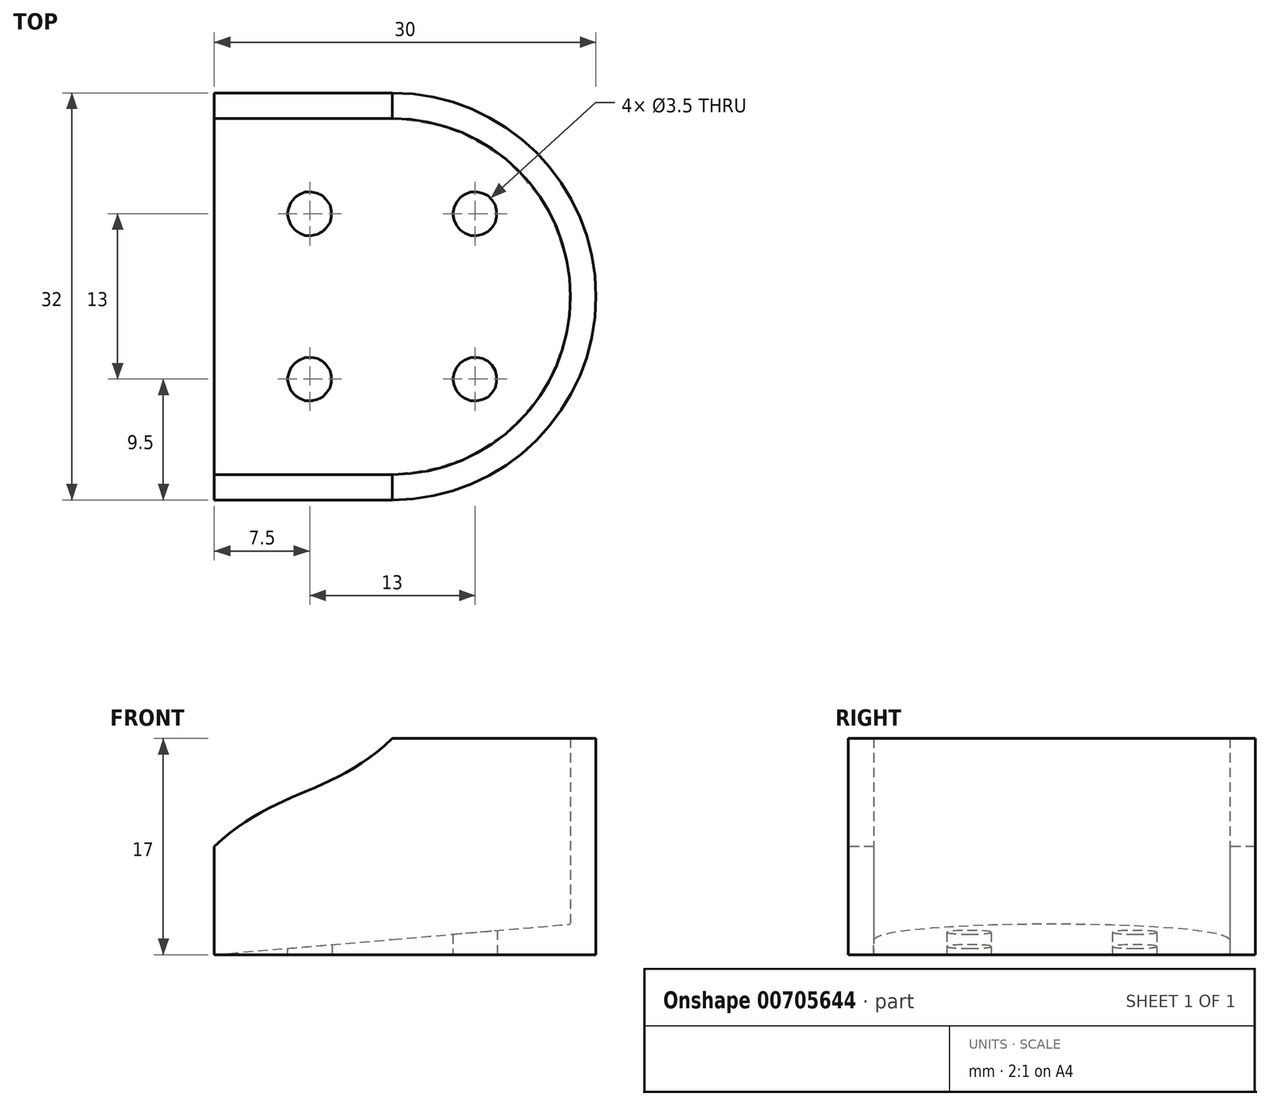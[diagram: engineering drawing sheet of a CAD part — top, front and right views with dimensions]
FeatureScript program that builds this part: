
annotation { "Feature Type Name" : "Feature", "Feature Type Description" : "" }
export const myFeature = defineFeature(function(context is Context, id is Id, definition is map)
    precondition{}
    {
        {
            var Q0;
            Q0=qCreatedBy(makeId("Top.planeOp"),FACE);
            var sketch = newSketch(context, id + "F0", { "sketchPlane" : qUnion([Q0])});
            skArc(sketch, "E0", {"start": v(0, -14) * mm, "mid": v(14, 0) * mm, "end": v(0, 14) * mm});
            skArc(sketch, "E1.0", {"start": v(0, -16) * mm, "mid": v(16, 0) * mm, "end": v(0, 16) * mm});
            skLineSegment(sketch, "E2", {"start": v(0, -16) * mm, "end": v(0, 16) * mm});
            skLineSegment(sketch, "E3", {"start": v(14, 0) * mm, "end": v(-14, 0) * mm});
            skPoint(sketch, "E3.startSnap0", {"position": v(16, 0) * mm});
            skLineSegment(sketch, "E4", {"start": v(-14, 14) * mm, "end": v(-14, 16) * mm});
            skLineSegment(sketch, "E5", {"start": v(-14, 16) * mm, "end": v(0, 16) * mm});
            skLineSegment(sketch, "E6", {"start": v(0, 14) * mm, "end": v(-14, 14) * mm});
            skLineSegment(sketch, "E7", {"start": v(0, -16) * mm, "end": v(-14, -16) * mm});
            skLineSegment(sketch, "E8", {"start": v(0, -14) * mm, "end": v(-14, -14) * mm});
            skLineSegment(sketch, "E9", {"start": v(-14, -14) * mm, "end": v(-14, -16) * mm});
            skLineSegment(sketch, "E10", {"start": v(-14, -14) * mm, "end": v(-14, 14) * mm});
            skLineSegment(sketch, "E11.bottom", {"start": v(6.5, 6.5) * mm, "end": v(-6.5, 6.5) * mm});
            skLineSegment(sketch, "E11.top", {"start": v(6.5, -6.5) * mm, "end": v(-6.5, -6.5) * mm});
            skLineSegment(sketch, "E11.left", {"start": v(6.5, 6.5) * mm, "end": v(6.5, -6.5) * mm});
            skLineSegment(sketch, "E11.right", {"start": v(-6.5, 6.5) * mm, "end": v(-6.5, -6.5) * mm});
            skCircle(sketch, "E12", {"center": v(6.5, 6.5) * mm, "radius": 1.75 * mm});
            skCircle(sketch, "E13", {"center": v(6.5, -6.5) * mm, "radius": 1.75 * mm});
            skCircle(sketch, "E14", {"center": v(-6.5, -6.5) * mm, "radius": 1.75 * mm});
            skCircle(sketch, "E15", {"center": v(-6.5, 6.5) * mm, "radius": 1.75 * mm});
            skSolve(sketch);
        }
        {
            var Q0;
            {var subQ3=sQuery(id+"F0.wireOp",EDGE,"E1.0");Q0=makeQuery(id+"F0.imprint","IMPRINT",FACE,{"disambiguationData":[TD([[makeQuery(id+"F0.imprint","IMPRINT",EDGE,{"derivedFrom":subQ3}),1.0]])]});}
            var Q1;
            {var subQ2=sQuery(id+"F0.wireOp",EDGE,"E7");Q1=makeQuery(id+"F0.imprint","IMPRINT",FACE,{"disambiguationData":[TD([[makeQuery(id+"F0.imprint","IMPRINT",EDGE,{"derivedFrom":subQ2}),-1.0]])]});}
            var Q2;
            Q2=makeQuery(id+"F0.imprint","IMPRINT",FACE,{"disambiguationData":[TD([[makeQuery(id+"F0.imprint","IMPRINT",EDGE,{"derivedFrom":sQuery(id+"F0.wireOp",EDGE,"E4")}),-1.0]])]});
            extrude(context, id + "F1", {"entities" : qUnion([Q0, Q1, Q2]), "depth" : 17 * mm, "offsetDistance" : 25 * mm});
        }
        {
            var Q0;
            Q0=makeQuery(id+"F1.opExtrude","SWEPT_FACE",FACE,{"disambiguationData":[OSD([sQuery(id+"F0.wireOp",EDGE,"E7")])]});
            var sketch = newSketch(context, id + "F2", { "sketchPlane" : qUnion([Q0])});
            skFitSpline(sketch, "E16", {"points": [v(0, 17) * mm, v(-14, 8.5) * mm], "startDerivative": vector(-14, -13.5) * mm, "endDerivative": vector(-14, -13.5) * mm});
            skSolve(sketch);
        }
        {
            var Q0;
            {var subQ0=sQuery(id+"F2.wireOp",EDGE,"E16");Q0=makeQuery(id+"F2.imprint","IMPRINT",FACE,{"disambiguationData":[TD([[makeQuery(id+"F2.imprint","IMPRINT",EDGE,{"derivedFrom":subQ0}),-1.0]])]});}
            extrude(context, id + "F3", {"entities" : qUnion([Q0]), "operationType" : NewBodyOperationType.REMOVE, "endBound" : BoundingType.THROUGH_ALL, "oppositeDirection" : true, "depth" : 25 * mm, "offsetDistance" : 25 * mm});
        }
        {
            var Q0;
            {var subQ3=sQuery(id+"F0.wireOp",EDGE,"E6");Q0=makeQuery(id+"F0.imprint","IMPRINT",FACE,{"disambiguationData":[TD([[makeQuery(id+"F0.imprint","IMPRINT",EDGE,{"derivedFrom":subQ3}),1.0]])]});}
            var Q1;
            {var subQ0=sQuery(id+"F0.wireOp",EDGE,"E3");var subQ1=sQuery(id+"F0.wireOp",EDGE,"E2");var subQ2=makeQuery(id+"F0.imprint","INTERSECT",VERTEX,{"derivedFrom":[subQ1,subQ0]});Q1=makeQuery(id+"F0.imprint","IMPRINT",FACE,{"disambiguationData":[TD([[makeQuery(id+"F0.imprint","IMPRINT",EDGE,{"disambiguationData":[TD([[subQ2,-1.0]])],"derivedFrom":subQ1}),-1.0]])]});}
            var Q2;
            {var subQ0=sQuery(id+"F0.wireOp",EDGE,"E3");var subQ1=sQuery(id+"F0.wireOp",EDGE,"E0");var subQ2=makeQuery(id+"F0.imprint","INTERSECT",VERTEX,{"derivedFrom":[subQ1,subQ0]});Q2=makeQuery(id+"F0.imprint","IMPRINT",FACE,{"disambiguationData":[TD([[makeQuery(id+"F0.imprint","IMPRINT",EDGE,{"disambiguationData":[TD([[subQ2,-1.0]])],"derivedFrom":subQ0}),-1.0]])]});}
            var Q3;
            {var subQ0=sQuery(id+"F0.wireOp",EDGE,"E3");var subQ1=sQuery(id+"F0.wireOp",EDGE,"E2");var subQ2=makeQuery(id+"F0.imprint","INTERSECT",VERTEX,{"derivedFrom":[subQ1,subQ0]});Q3=makeQuery(id+"F0.imprint","IMPRINT",FACE,{"disambiguationData":[TD([[makeQuery(id+"F0.imprint","IMPRINT",EDGE,{"disambiguationData":[TD([[subQ2,-1.0]])],"derivedFrom":subQ1}),1.0]])]});}
            var Q4;
            {var subQ0=sQuery(id+"F0.wireOp",EDGE,"E11.top");var subQ1=sQuery(id+"F0.wireOp",EDGE,"E2");var subQ2=makeQuery(id+"F0.imprint","INTERSECT",VERTEX,{"derivedFrom":[subQ1,subQ0]});Q4=makeQuery(id+"F0.imprint","IMPRINT",FACE,{"disambiguationData":[TD([[makeQuery(id+"F0.imprint","IMPRINT",EDGE,{"disambiguationData":[TD([[subQ2,-1.0]])],"derivedFrom":subQ1}),-1.0]])]});}
            var Q5;
            {var subQ0=sQuery(id+"F0.wireOp",EDGE,"E11.top");var subQ1=sQuery(id+"F0.wireOp",EDGE,"E2");var subQ2=makeQuery(id+"F0.imprint","INTERSECT",VERTEX,{"derivedFrom":[subQ1,subQ0]});Q5=makeQuery(id+"F0.imprint","IMPRINT",FACE,{"disambiguationData":[TD([[makeQuery(id+"F0.imprint","IMPRINT",EDGE,{"disambiguationData":[TD([[subQ2,-1.0]])],"derivedFrom":subQ1}),1.0]])]});}
            var Q6;
            {var subQ0=sQuery(id+"F0.wireOp",EDGE,"E8");Q6=makeQuery(id+"F0.imprint","IMPRINT",FACE,{"disambiguationData":[TD([[makeQuery(id+"F0.imprint","IMPRINT",EDGE,{"derivedFrom":subQ0}),-1.0]])]});}
            var Q7;
            {var subQ5=sQuery(id+"F0.wireOp",EDGE,"E3");var subQ6=sQuery(id+"F0.wireOp",EDGE,"E0");var subQ7=makeQuery(id+"F0.imprint","INTERSECT",VERTEX,{"derivedFrom":[subQ6,subQ5]});Q7=makeQuery(id+"F0.imprint","IMPRINT",FACE,{"disambiguationData":[TD([[makeQuery(id+"F0.imprint","IMPRINT",EDGE,{"disambiguationData":[TD([[subQ7,-1.0]])],"derivedFrom":subQ5}),1.0]])]});}
            extrude(context, id + "F4", {"entities" : qUnion([Q0, Q1, Q2, Q3, Q4, Q5, Q6, Q7]), "operationType" : NewBodyOperationType.ADD, "depth" : 2.4 * mm, "offsetDistance" : 25 * mm});
        }
        {
            var Q0;
            Q0=makeQuery(id+"F4.opExtrude","CAP_EDGE",EDGE,{"disambiguationData":[OSD([sQuery(id+"F0.wireOp",EDGE,"E10")])],"isStart":false});
            chamfer(context, id + "F5", {"entities" : qUnion([Q0]), "chamferType" : ChamferType.TWO_OFFSETS, "width1" : 2.4 * mm, "oppositeDirection" : false, "width2" : 28 * mm, "tangentPropagation" : true});
        }
    });
